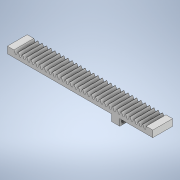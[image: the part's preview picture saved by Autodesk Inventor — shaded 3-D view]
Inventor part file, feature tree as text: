
AUTODESK INVENTOR PART (.ipt)
format: ipt  version: 2021 (Build 250183000, 183)  size: 285,184 bytes
history: native  units: mm
features: sketch x5, extrude x5, pattern_linear x1
ambient origin geometry x8: Origin, YZ Plane, XZ Plane, XY Plane, X Axis, Y Axis, Z Axis, Center Point
bodies: Body1 (feature_tree)
feature tree (11):
  sketch  "Sketch1"  dims[d16=168.0mm d17=8.0mm]
  extrude  "Extrusion4"  Depth=8.0mm
  extrude  "Extrusion5"  Depth=8.0mm TaperAngle=0.0deg
  pattern_linear  "Rectangular Pattern1"  Count1=31 Spacing1=5.2mm
  extrude  "Extrusion6"  Depth=10.0mm
  extrude  "Extrusion7"  Depth=40.0mm
  extrude  "Extrusion8"  Depth=8.0mm TaperAngle=0.0deg
  sketch  "Sketch3"  dims[d18=8.0mm d19=24.0mm d20=0.0mm]
  sketch  "Sketch4"  dims[d21=0.0mm d22=0.0mm d23=310.0mm d25=5.2mm]
  sketch  "Sketch5"  dims[d26=8.0mm d27=0.0mm d28=10.0mm]
  sketch  "Sketch6"  dims[d29=24.0mm d30=40.0mm d31=8.0mm d32=0.0mm d33=4.1mm d34=4.1mm d35=4.0mm d36=4.0mm d37=4.0mm d38=4.0mm d39=8.0mm d40=0.0mm]
